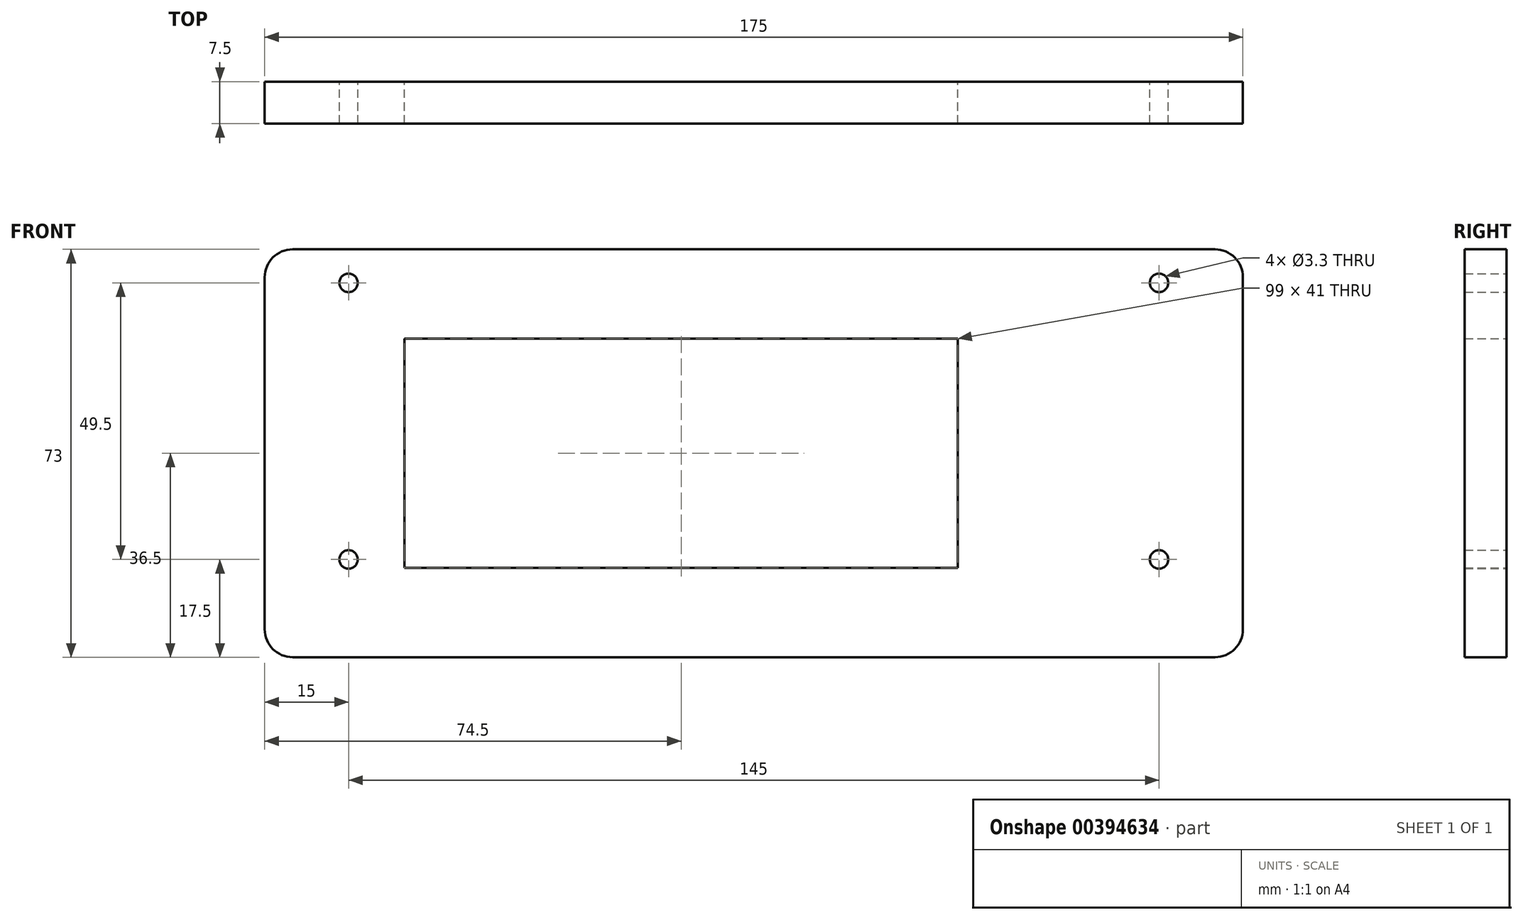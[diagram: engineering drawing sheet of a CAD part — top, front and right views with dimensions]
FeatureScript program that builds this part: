
annotation { "Feature Type Name" : "Feature", "Feature Type Description" : "" }
export const myFeature = defineFeature(function(context is Context, id is Id, definition is map)
    precondition{}
    {
        {
            var Q0;
            Q0=qCreatedBy(makeId("Front.planeOp"),FACE);
            var sketch = newSketch(context, id + "F0", { "sketchPlane" : qUnion([Q0])});
            skLineSegment(sketch, "E0.bottom", {"start": v(87.5, -36.5) * mm, "end": v(-87.5, -36.5) * mm});
            skLineSegment(sketch, "E0.top", {"start": v(87.5, 36.5) * mm, "end": v(-87.5, 36.5) * mm});
            skLineSegment(sketch, "E0.left", {"start": v(87.5, -36.5) * mm, "end": v(87.5, 36.5) * mm});
            skLineSegment(sketch, "E0.right", {"start": v(-87.5, -36.5) * mm, "end": v(-87.5, 36.5) * mm});
            skPoint(sketch, "E0.middle", {"position": v(0, 0) * mm});
            skLineSegment(sketch, "E1.bottom", {"start": v(-62.5, 20.5) * mm, "end": v(36.5, 20.5) * mm});
            skLineSegment(sketch, "E1.top", {"start": v(-62.5, -20.5) * mm, "end": v(36.5, -20.5) * mm});
            skLineSegment(sketch, "E1.left", {"start": v(-62.5, 20.5) * mm, "end": v(-62.5, -20.5) * mm});
            skLineSegment(sketch, "E1.right", {"start": v(36.5, 20.5) * mm, "end": v(36.5, -20.5) * mm});
            skPoint(sketch, "E2", {"position": v(-72.5, 30.5) * mm});
            skPoint(sketch, "E3", {"position": v(72.5, 30.5) * mm});
            skPoint(sketch, "E4", {"position": v(-72.5, -19) * mm});
            skPoint(sketch, "E5", {"position": v(72.5, -19) * mm});
            skLineSegment(sketch, "E6", {"start": v(-72.5, -36.5) * mm, "end": v(-72.5, 36.5) * mm, "construction": true});
            skLineSegment(sketch, "E7", {"start": v(-87.5, 30.5) * mm, "end": v(87.5, 30.5) * mm, "construction": true});
            skLineSegment(sketch, "E8", {"start": v(72.5, 36.5) * mm, "end": v(72.5, -36.5) * mm, "construction": true});
            skLineSegment(sketch, "E9", {"start": v(-87.5, -19) * mm, "end": v(87.5, -19) * mm, "construction": true});
            skSolve(sketch);
        }
        {
            var Q0;
            Q0=makeQuery(id+"F0.imprint","IMPRINT",FACE,{"disambiguationData":[TD([[makeQuery(id+"F0.imprint","IMPRINT",EDGE,{"derivedFrom":sQuery(id+"F0.wireOp",EDGE,"E0.bottom")}),-1.0]])]});
            extrude(context, id + "F1", {"entities" : qUnion([Q0]), "depth" : 7.5 * mm, "offsetDistance" : 25 * mm});
        }
        {
            var Q0;
            Q0=makeQuery(id+"F1.opExtrude","SWEPT_EDGE",EDGE,{"disambiguationData":[OSD([sQuery(id+"F0.wireOp",EDGE,"E0.top"),sQuery(id+"F0.wireOp",EDGE,"E0.right")])]});
            var Q1;
            Q1=makeQuery(id+"F1.opExtrude","SWEPT_EDGE",EDGE,{"disambiguationData":[OSD([sQuery(id+"F0.wireOp",EDGE,"E0.top"),sQuery(id+"F0.wireOp",EDGE,"E0.left")])]});
            var Q2;
            Q2=makeQuery(id+"F1.opExtrude","SWEPT_EDGE",EDGE,{"disambiguationData":[OSD([sQuery(id+"F0.wireOp",EDGE,"E0.bottom"),sQuery(id+"F0.wireOp",EDGE,"E0.left")])]});
            var Q3;
            Q3=makeQuery(id+"F1.opExtrude","SWEPT_EDGE",EDGE,{"disambiguationData":[OSD([sQuery(id+"F0.wireOp",EDGE,"E0.bottom"),sQuery(id+"F0.wireOp",EDGE,"E0.right")])]});
            fillet(context, id + "F2", {"entities" : qUnion([Q0, Q1, Q2, Q3]), "radius" : 5 * mm, "tangentPropagation" : true, "allowEdgeOverflow" : false});
        }
        {
            var Q0;
            Q0=sQuery(id+"F0.wireOp",VERTEX,"E2");
            var Q1;
            Q1=sQuery(id+"F0.wireOp",VERTEX,"E4");
            var Q2;
            Q2=sQuery(id+"F0.wireOp",VERTEX,"E5");
            var Q3;
            Q3=sQuery(id+"F0.wireOp",VERTEX,"E3");
            var Q4;
            Q4=makeQuery(id+"F1.opExtrude","SWEPT_BODY",BODY,{"disambiguationData":[OSD([sQuery(id+"F0.wireOp",EDGE,"E0.bottom"),sQuery(id+"F0.wireOp",EDGE,"E0.top"),sQuery(id+"F0.wireOp",EDGE,"E0.left"),sQuery(id+"F0.wireOp",EDGE,"E0.right"),sQuery(id+"F0.wireOp",EDGE,"E1.bottom"),sQuery(id+"F0.wireOp",EDGE,"E1.top"),sQuery(id+"F0.wireOp",EDGE,"E1.left"),sQuery(id+"F0.wireOp",EDGE,"E1.right")])]});
            hole(context, id + "F3", {"style" : HoleStyle.SIMPLE, "endStyle" : HoleEndStyle.THROUGH, "oppositeDirection" : true, "standardTappedOrClearance" : lookupTablePath({ "standard" : "ISO", "fit" : "Normal", "size" : "M3", "type" : "Clearance" }), "standardBlindInLast" : lookupTablePath({ "fit" : "Standard", "standard" : "ISO", "size" : "M3", "type" : "Clearance" }), "holeDiameter" : 3.3 * mm, "majorDiameter" : 5 * mm, "isTappedThrough" : true, "tappedDepth" : 12 * mm, "tapClearance" : 3, "locations" : qUnion([Q0, Q1, Q2, Q3]), "scope" : qUnion([Q4])});
        }
    });
